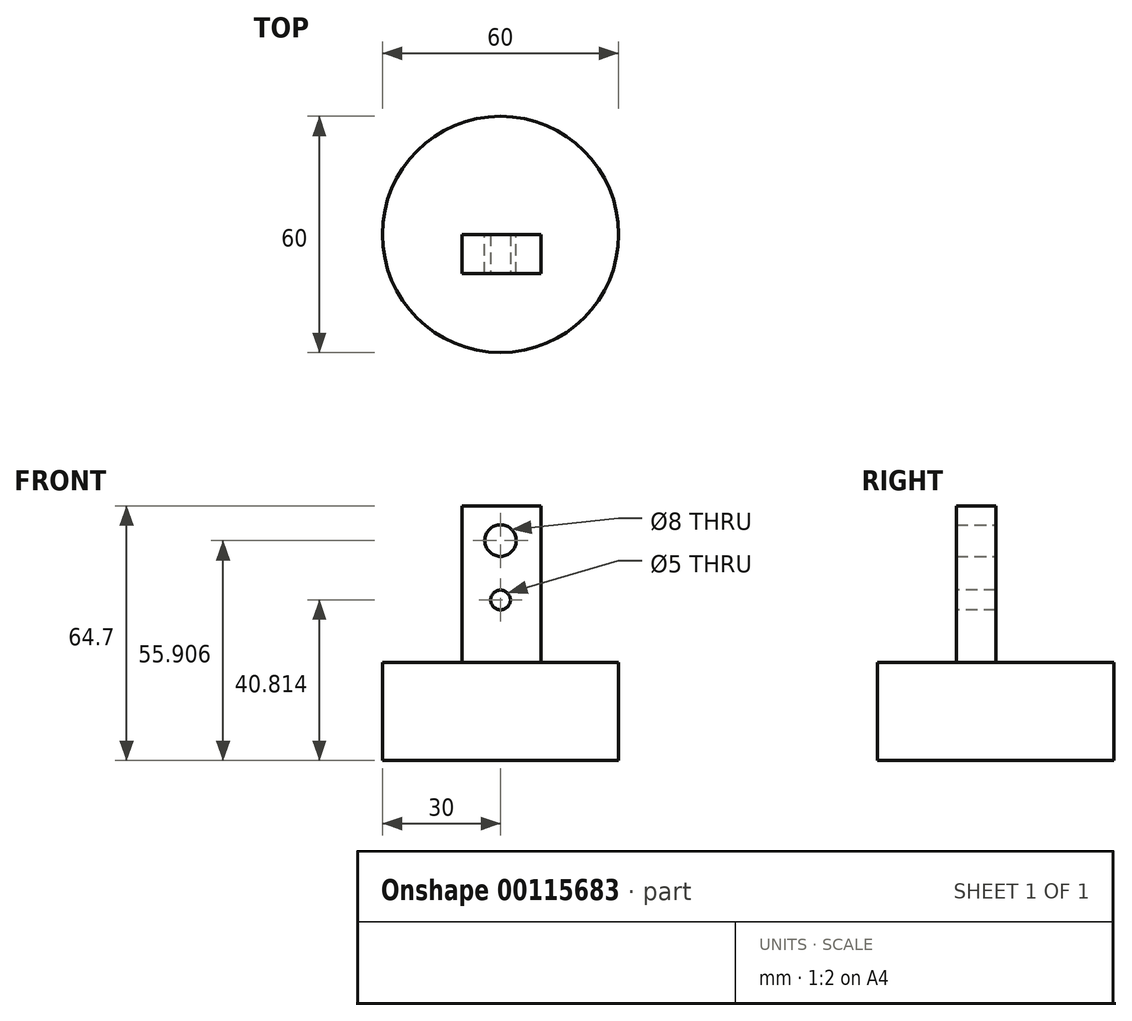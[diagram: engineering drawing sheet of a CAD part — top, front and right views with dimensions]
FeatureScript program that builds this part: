
annotation { "Feature Type Name" : "Feature", "Feature Type Description" : "" }
export const myFeature = defineFeature(function(context is Context, id is Id, definition is map)
    precondition{}
    {
        {
            var Q0;
            Q0=qCreatedBy(makeId("Top.planeOp"),FACE);
            var sketch = newSketch(context, id + "F0", { "sketchPlane" : qUnion([Q0])});
            skCircle(sketch, "E0", {"center": v(0, 0) * mm, "radius": 30 * mm});
            skSolve(sketch);
        }
        {
            var Q0;
            Q0 = qSketchRegion(id + "F0", true);
            extrude(context, id + "F1", {"entities" : qUnion([Q0]), "depth" : 25 * mm});
        }
        {
            var Q0;
            Q0=makeQuery(id+"F1.opExtrude","CAP_FACE",FACE,{"disambiguationData":[OSD([sQuery(id+"F0.wireOp",EDGE,"E0")])],"isStart":false});
            var sketch = newSketch(context, id + "F2", { "sketchPlane" : qUnion([Q0])});
            skLineSegment(sketch, "E1.bottom", {"start": v(-9.76, -10) * mm, "end": v(10.24, -10) * mm});
            skLineSegment(sketch, "E1.top", {"start": v(-9.76, 0) * mm, "end": v(10.24, 0) * mm});
            skLineSegment(sketch, "E1.left", {"start": v(-9.76, -10) * mm, "end": v(-9.76, 0) * mm});
            skLineSegment(sketch, "E1.right", {"start": v(10.24, -10) * mm, "end": v(10.24, 0) * mm});
            skSolve(sketch);
        }
        {
            var Q0;
            Q0 = qSketchRegion(id + "F2", true);
            extrude(context, id + "F3", {"entities" : qUnion([Q0]), "operationType" : NewBodyOperationType.ADD, "depth" : 39.7 * mm});
        }
        {
            var Q0;
            Q0=makeQuery(id+"F3.opExtrude","SWEPT_FACE",FACE,{"disambiguationData":[OSD([sQuery(id+"F2.wireOp",EDGE,"E1.top")])]});
            var sketch = newSketch(context, id + "F4", { "sketchPlane" : qUnion([Q0])});
            skCircle(sketch, "E2", {"center": v(0, 55.9) * mm, "radius": 4 * mm});
            skSolve(sketch);
        }
        {
            var Q0;
            Q0 = qSketchRegion(id + "F4", true);
            extrude(context, id + "F5", {"entities" : qUnion([Q0]), "operationType" : NewBodyOperationType.REMOVE, "oppositeDirection" : true, "depth" : 41.2 * mm});
        }
        {
            var Q0;
            Q0=makeQuery(id+"F3.opExtrude","SWEPT_FACE",FACE,{"disambiguationData":[OSD([sQuery(id+"F2.wireOp",EDGE,"E1.bottom")])]});
            var sketch = newSketch(context, id + "F6", { "sketchPlane" : qUnion([Q0])});
            skPoint(sketch, "E3", {"position": v(0, 40.81) * mm});
            skSolve(sketch);
        }
        {
            var Q0;
            Q0=sQuery(id+"F6.wireOp",VERTEX,"E3");
            var Q1;
            Q1=makeQuery(id+"F1.opExtrude","SWEPT_BODY",BODY,{"disambiguationData":[OSD([sQuery(id+"F0.wireOp",EDGE,"E0")])]});
            hole(context, id + "F7", {"style" : HoleStyle.SIMPLE, "endStyle" : HoleEndStyle.THROUGH, "holeDiameter" : 5 * mm, "isTappedThrough" : true, "tappedDepth" : 12 * mm, "tapClearance" : 3, "locations" : qUnion([Q0]), "scope" : qUnion([Q1])});
        }
    });
